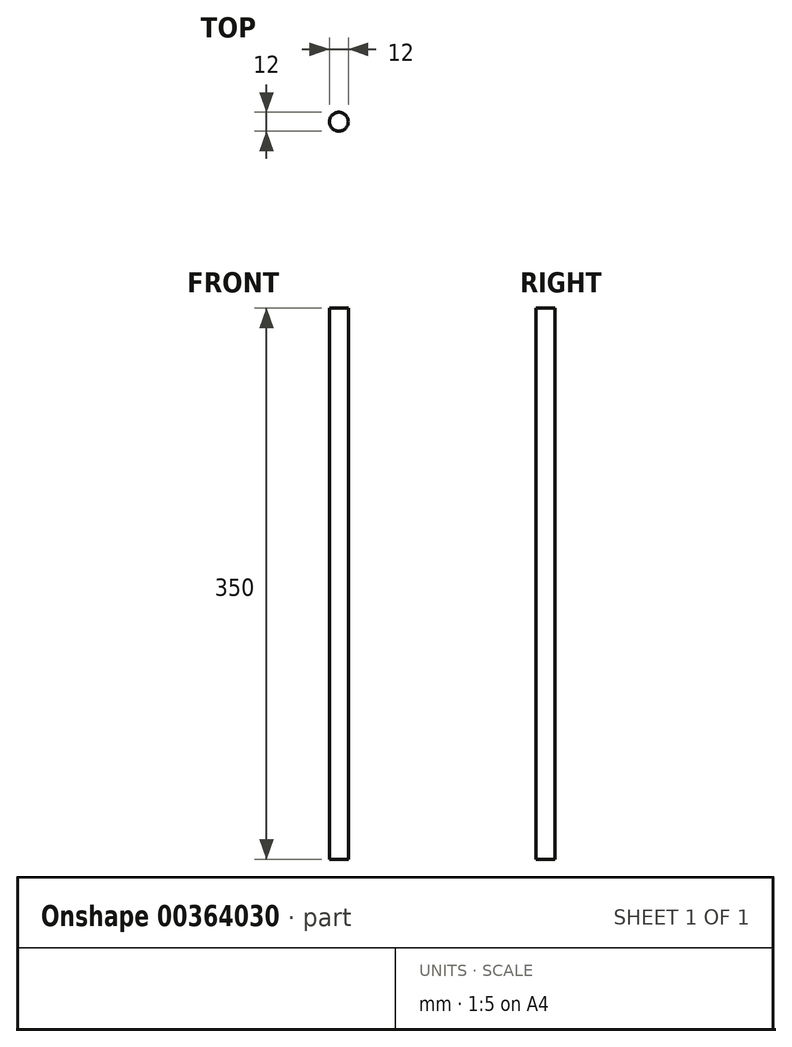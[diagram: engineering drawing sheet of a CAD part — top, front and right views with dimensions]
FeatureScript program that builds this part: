
annotation { "Feature Type Name" : "Feature", "Feature Type Description" : "" }
export const myFeature = defineFeature(function(context is Context, id is Id, definition is map)
    precondition{}
    {
        {
            var Q0;
            Q0=qCreatedBy(makeId("Top.planeOp"),FACE);
            var sketch = newSketch(context, id + "F0", { "sketchPlane" : qUnion([Q0])});
            skCircle(sketch, "E0", {"center": v(0, 0) * mm, "radius": 6 * mm});
            skSolve(sketch);
        }
        {
            var Q0;
            Q0 = qSketchRegion(id + "F0", true);
            extrude(context, id + "F1", {"entities" : qUnion([Q0]), "depth" : 350 * mm});
        }
    });
